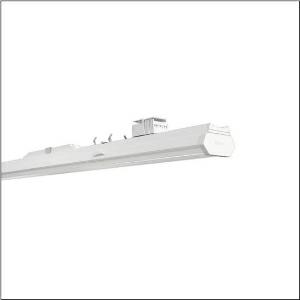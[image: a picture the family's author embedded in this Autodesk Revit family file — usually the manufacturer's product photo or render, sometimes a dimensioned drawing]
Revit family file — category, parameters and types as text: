
# Revit family: licross_21_protected_mo_52td1bmn4axg
name_source: partatom
category: Lighting Fixtures
units: mm (PartAtom-declared; Revit-internal decimal feet)

## family parameters
Cut with Voids When Loaded = No
Host = Face
Light Source = No
Part Type = Normal
Room Calculation Point = No
Round Connector Dimension = Use Diameter
Shared = No

## types (1)
- --- (1 x LED, 10100 lm, 60.5 W, 4000K)
    Apparent Load = 61 VA
    CIE Flux Codes = 54 82 95 97 100
    Color Rendering = 80
    Color Temperature = 4000K
    Default Elevation = 1800 mm
    Description = Licross 21 Protected MO, luminaire insert, of sheet steel, galvanised, coil coated, white, length: 1.500mm, width: 90mm, height: 103mm, LED rated luminous flux: 10.100lm, light colour: 840, SDCM (Standard Deviation of Colour Matching)MacAdam ≤ 3 SDCM (initial), control gear: ON/OFF Multilumen, with plug, 3-pole, with phase selection, mains connection: 220..240V, AC, 50/60Hz, rated input power: 61W, internal wiring halogen-free, primary optical cover: cover, of PMMA, light emission: direct distribution, primary light characteristic: symmetric, protection rating (complete): IP54, insulation class (complete): insulation class I (protective earthing), certification: CE, ENEC, VDE, UKCA, protection symbol: D if used in an environment with non-conductive dust loads with corresponding accessories, impact resistance: IK06, permissible ambient temperature for indoor applications: -35..+45°C, corresponds to IFS (International Featured Standards) requirements for safety and quality in the food industry, reducing of maximum allowable ambient temperature of 5°C with ceiling mounting, LABS conformity tested according to VDMA 24364:2018-05, The light source and the operating device comply with the requirements of the Ecodesign Regulation (EU) 2019/2020 and are replaceable in accordance with this regulation, packaging unit: 1 piece
    Height = 92 mm
    Lamp = 1 x LED
    Lamp Light Flux = 10100 lm
    Lamp Power = 60.5 W
    Lamp count = 1
    Length = 1500 mm
    Luminous efficacy = 167 lm/W
    Manufacturer = Siteco
    ModVariant = No
    Model = 52TD1BMN4AXG
    Mounting Place = Ceiling
    Mounting Type = Pendant
    Number of Poles = 1
    OnlyDefault = Yes
    Power Factor = 1
    Product Name = Licross 21 Protected MO
    Product group = luminaire insert | ceiling pendant
    ProductGroupID = 901
    Protection Class = Protection class I
    Protection Degree = IP 54
    RLX_Detail_Level = 1
    RLX_Emergency_Light_Flux = 0 lm
    RLX_Emergency_Type = 0
    RLX_Emergency_Type_DB = No
    RlxData = <blob elided: 22301 chars, md5=57a5ffcf>
    Socket = socket
    Standby Power = 0 W
    System Light Flux = 10100 lm
    System Power = 61 W
    Type Comments = factory setting: luminous flux: 100 % | (A | C | E) | 140 mA
    Type Image = l_1256148.jpg
    URL = http://relux.com
    VarID = @adj_109137
    Voltage = 0 V
    Weight = 0.00 kg
    Width = 88 mm

## geometry (parser evidence)
native form markers: Blend x4, Sweep x10
no freeform markers — native parametric forms only
